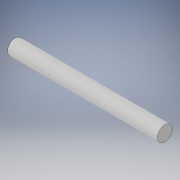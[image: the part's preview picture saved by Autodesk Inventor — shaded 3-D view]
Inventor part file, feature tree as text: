
AUTODESK INVENTOR PART (.ipt)
format: ipt  version: 2019 (Build 230136000, 136)  size: 89,088 bytes
history: native  units: in
note: dims shown in document units (in); Inventor stores cm internally (conversion verified against a paired STEP export)
features: extrude x1, sketch x1
ambient origin geometry x8: Origin, YZ Plane, XZ Plane, XY Plane, X Axis, Y Axis, Z Axis, Center Point
bodies: Solid1 (feature_tree)
feature tree (2):
  extrude  "Extrusion1"  Depth=3.937in TaperAngle=0.0deg
  sketch  "Sketch1"  dims[d0=0.3937in d1=3.937in d2=0.0in]
